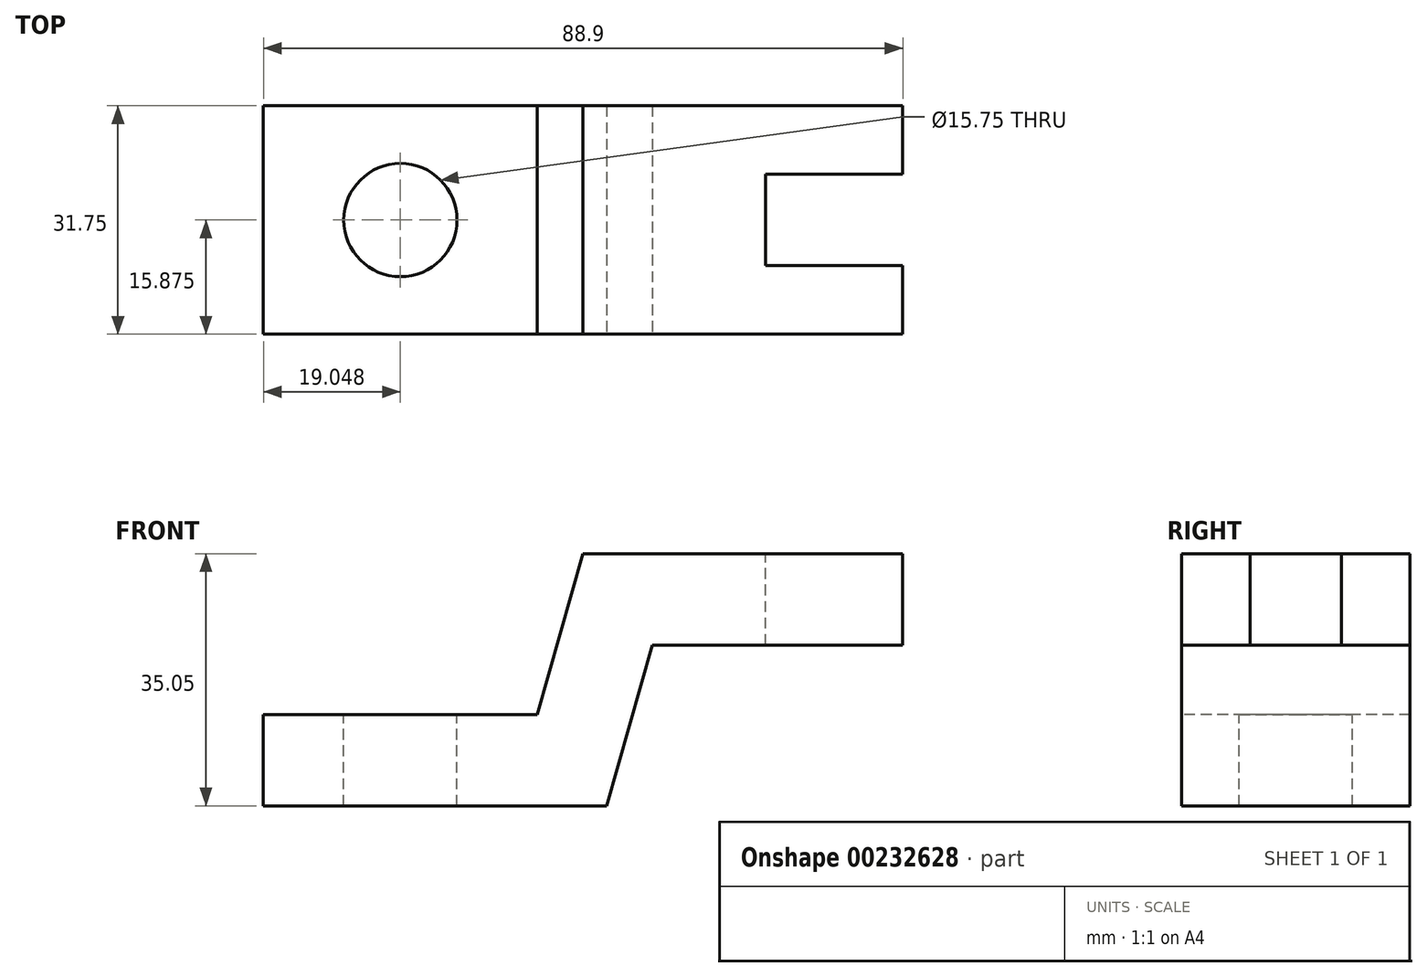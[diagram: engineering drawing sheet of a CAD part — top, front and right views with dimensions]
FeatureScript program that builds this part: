
annotation { "Feature Type Name" : "Feature", "Feature Type Description" : "" }
export const myFeature = defineFeature(function(context is Context, id is Id, definition is map)
    precondition{}
    {
        {
            var Q0;
            Q0=qCreatedBy(makeId("Front.planeOp"),FACE);
            var sketch = newSketch(context, id + "F0", { "sketchPlane" : qUnion([Q0])});
            skLineSegment(sketch, "E0", {"start": v(0, 0) * mm, "end": v(-47.75, 0) * mm});
            skLineSegment(sketch, "E1", {"start": v(-47.75, 0) * mm, "end": v(-47.75, 12.7) * mm});
            skLineSegment(sketch, "E2", {"start": v(-47.75, 12.7) * mm, "end": v(-9.65, 12.7) * mm});
            skLineSegment(sketch, "E3", {"start": v(41.15, 22.35) * mm, "end": v(41.15, 35.05) * mm});
            skLineSegment(sketch, "E4", {"start": v(-3.3, 35.05) * mm, "end": v(41.15, 35.05) * mm});
            skLineSegment(sketch, "E5", {"start": v(-3.3, 35.05) * mm, "end": v(-9.65, 12.7) * mm});
            skLineSegment(sketch, "E6", {"start": v(41.15, 22.35) * mm, "end": v(6.35, 22.35) * mm});
            skLineSegment(sketch, "E7", {"start": v(0, 0) * mm, "end": v(6.35, 22.35) * mm});
            skSolve(sketch);
        }
        {
            var Q0;
            Q0 = qSketchRegion(id + "F0", true);
            extrude(context, id + "F1", {"entities" : qUnion([Q0]), "oppositeDirection" : true, "depth" : 31.75 * mm});
        }
        {
            var Q0;
            Q0=makeQuery(id+"F1.opExtrude","SWEPT_FACE",FACE,{"disambiguationData":[OSD([sQuery(id+"F0.wireOp",EDGE,"E4")])]});
            var sketch = newSketch(context, id + "F2", { "sketchPlane" : qUnion([Q0])});
            skLineSegment(sketch, "E8", {"start": v(41.15, 22.23) * mm, "end": v(22.1, 22.23) * mm});
            skLineSegment(sketch, "E9", {"start": v(22.1, 22.22) * mm, "end": v(22.1, 9.52) * mm});
            skLineSegment(sketch, "E10", {"start": v(22.1, 9.52) * mm, "end": v(41.15, 9.52) * mm});
            skLineSegment(sketch, "E11", {"start": v(41.15, 9.52) * mm, "end": v(41.15, 22.23) * mm});
            skSolve(sketch);
        }
        {
            var Q0;
            Q0 = qSketchRegion(id + "F2", true);
            extrude(context, id + "F3", {"entities" : qUnion([Q0]), "operationType" : NewBodyOperationType.REMOVE, "oppositeDirection" : true, "depth" : 25.4 * mm});
        }
        {
            var Q0;
            Q0=makeQuery(id+"F1.opExtrude","SWEPT_FACE",FACE,{"disambiguationData":[OSD([sQuery(id+"F0.wireOp",EDGE,"E2")])]});
            var sketch = newSketch(context, id + "F4", { "sketchPlane" : qUnion([Q0])});
            skCircle(sketch, "E12", {"center": v(-28.7, 15.88) * mm, "radius": 7.87 * mm});
            skSolve(sketch);
        }
        {
            var Q0;
            Q0 = qSketchRegion(id + "F4", true);
            extrude(context, id + "F5", {"entities" : qUnion([Q0]), "operationType" : NewBodyOperationType.REMOVE, "oppositeDirection" : true, "depth" : 25.4 * mm});
        }
    });
